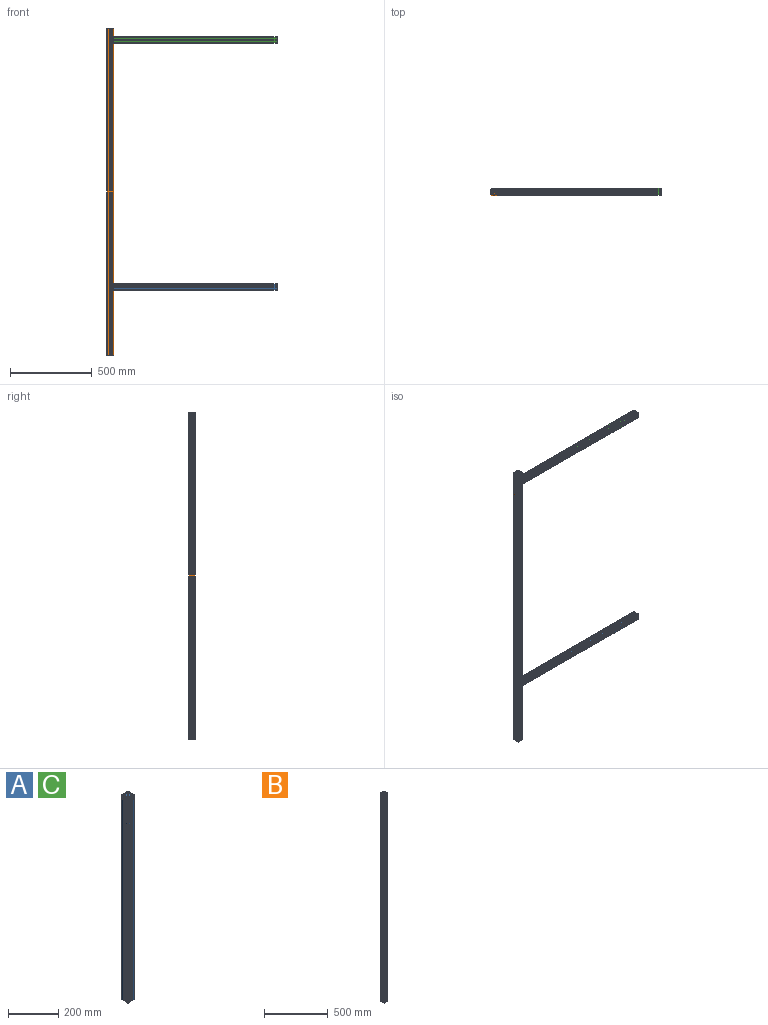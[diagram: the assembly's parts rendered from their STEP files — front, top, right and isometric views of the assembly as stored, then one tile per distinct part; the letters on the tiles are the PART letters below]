
ASSEMBLY  parts=3 mates=2
PART A: 147 faces, bbox 40x40x1000 mm
  f0: plane 1000x5.4mm, normal (1,0,0), area 5400mm2, adj f1,f7,f33,f146
  f1: cylinder r=0.5mm len=1000mm, axis (0,0,1), area 785.4mm2, adj f0,f2,f33,f146
  f2: plane 1000x5.4mm, normal (0,-1,0), area 5400mm2, adj f1,f3,f33,f146
  f3: cylinder r=0.5mm len=1000mm, axis (0,0,1), area 785.4mm2, adj f2,f4,f33,f146
  f4: plane 1000x3.7mm, normal (-1,0,0), area 3700mm2, adj f3,f5,f33,f146
  f5: cylinder r=2.2mm len=1000mm, axis (0,0,1), area 3455.8mm2, adj f4,f6,f33,f146
  f6: plane 1000x3.7mm, normal (0,1,0), area 3700mm2, adj f5,f7,f33,f146
  f7: cylinder r=0.5mm len=1000mm, axis (0,0,1), area 785.4mm2, adj f0,f6,f33,f146
  f8: plane 1000x5.4mm, normal (0,-1,0), area 5400mm2, adj f9,f15,f33,f146
  f9: cylinder r=0.5mm len=1000mm, axis (0,0,1), area 785.4mm2, adj f8,f10,f33,f146
  f10: plane 1000x5.4mm, normal (-1,0,0), area 5400mm2, adj f9,f11,f33,f146
  f11: cylinder r=0.5mm len=1000mm, axis (0,0,1), area 785.4mm2, adj f10,f12,f33,f146
  f12: plane 1000x3.7mm, normal (0,1,0), area 3700mm2, adj f11,f13,f33,f146
  f13: cylinder r=2.2mm len=1000mm, axis (0,0,1), area 3455.8mm2, adj f12,f14,f33,f146
  f14: plane 1000x3.7mm, normal (1,0,0), area 3700mm2, adj f13,f15,f33,f146
  f15: cylinder r=0.5mm len=1000mm, axis (0,0,1), area 785.4mm2, adj f8,f14,f33,f146
  f16: plane 1000x5.4mm, normal (-1,0,0), area 5400mm2, adj f17,f23,f33,f146
  f17: cylinder r=0.5mm len=1000mm, axis (0,0,1), area 785.4mm2, adj f16,f18,f33,f146
  f18: plane 1000x5.4mm, normal (0,1,0), area 5400mm2, adj f17,f19,f33,f146
  f19: cylinder r=0.5mm len=1000mm, axis (0,0,1), area 785.4mm2, adj f18,f20,f33,f146
  f20: plane 1000x3.7mm, normal (1,0,0), area 3700mm2, adj f19,f21,f33,f146
  f21: cylinder r=2.2mm len=1000mm, axis (0,0,1), area 3455.8mm2, adj f20,f22,f33,f146
  f22: plane 1000x3.7mm, normal (0,-1,0), area 3700mm2, adj f21,f23,f33,f146
  f23: cylinder r=0.5mm len=1000mm, axis (0,0,1), area 785.4mm2, adj f16,f22,f33,f146
  f24: plane 1000x5.4mm, normal (0,1,0), area 5400mm2, adj f25,f31,f33,f146
  f25: cylinder r=0.5mm len=1000mm, axis (0,0,1), area 785.4mm2, adj f24,f26,f33,f146
  f26: plane 1000x5.4mm, normal (1,0,0), area 5400mm2, adj f25,f27,f33,f146
  f27: cylinder r=0.5mm len=1000mm, axis (0,0,1), area 785.4mm2, adj f26,f28,f33,f146
  f28: plane 1000x3.7mm, normal (0,-1,0), area 3700mm2, adj f27,f29,f33,f146
  f29: cylinder r=2.2mm len=1000mm, axis (0,0,1), area 3455.8mm2, adj f28,f30,f33,f146
  f30: plane 1000x3.7mm, normal (-1,0,0), area 3700mm2, adj f29,f31,f33,f146
  f31: cylinder r=0.5mm len=1000mm, axis (0,0,1), area 785.4mm2, adj f24,f30,f33,f146
  f32: cylinder r=3.4mm len=1000mm, axis (0,0,1), area 21362.8mm2, adj f33,f146
  f33: plane 40x40mm, normal (0,0,-1), area 657.1mm2, adj f0,f1,f2,f3,f4,f5,f6,f7
  f34: cylinder r=1.5mm len=1000mm, axis (0,0,1), area 2356.2mm2, adj f33,f35,f145,f146
  f35: plane 1000x10.5mm, normal (-1,0,0), area 10500mm2, adj f33,f34,f36,f146
  f36: cylinder r=4mm len=1000mm, axis (0,0,1), area 6283.2mm2, adj f33,f35,f37,f146
  f37: plane 1000x10.5mm, normal (0,1,0), area 10500mm2, adj f33,f36,f38,f146
  f38: cylinder r=1.5mm len=1000mm, axis (0,0,1), area 2356.2mm2, adj f33,f37,f39,f146
  f39: plane 1000x2mm, normal (1,0,0), area 2000mm2, adj f33,f38,f40,f146
  f40: cylinder r=1mm len=1000mm, axis (0,0,1), area 1570.8mm2, adj f33,f39,f41,f146
  f41: plane 1000x1.5mm, normal (0,-1,0), area 1500mm2, adj f33,f40,f42,f146
  f42: cylinder r=0.5mm len=1000mm, axis (0,0,1), area 785.4mm2, adj f33,f41,f43,f146
  f43: plane 1000x1.5mm, normal (-1,0,0), area 1500mm2, adj f33,f42,f44,f146
  f44: cylinder r=0.5mm len=1000mm, axis (0,0,1), area 785.4mm2, adj f33,f43,f45,f146
  f45: cylinder r=2.5mm len=1000mm, axis (0,0,1), area 3927mm2, adj f33,f44,f46,f146
  f46: plane 1000x1.31mm, normal (1,0,0), area 1307.6mm2, adj f33,f45,f47,f146
  f47: cylinder r=5mm len=1000mm, axis (0,0,1), area 3927mm2, adj f33,f46,f48,f146
  f48: plane 1000x1.44mm, normal (0.71,0.71,0), area 2039.8mm2, adj f33,f47,f49,f146
  f49: cylinder r=5mm len=1000mm, axis (0,0,1), area 3927mm2, adj f33,f48,f50,f146
  f50: plane 1000x7.12mm, normal (0,1,0), area 7115.2mm2, adj f33,f49,f51,f146
  f51: cylinder r=5mm len=1000mm, axis (0,0,1), area 3927mm2, adj f33,f50,f52,f146
  f52: plane 1000x1.44mm, normal (-0.71,0.71,0), area 2039.8mm2, adj f33,f51,f53,f146
  f53: cylinder r=5mm len=1000mm, axis (0,0,1), area 3927mm2, adj f33,f52,f54,f146
  f54: plane 1000x1.31mm, normal (-1,0,0), area 1307.6mm2, adj f33,f53,f55,f146
  f55: cylinder r=2.5mm len=1000mm, axis (0,0,1), area 3927mm2, adj f33,f54,f56,f146
  f56: cylinder r=0.5mm len=1000mm, axis (0,0,1), area 785.4mm2, adj f33,f55,f57,f146
  f57: plane 1000x1.5mm, normal (1,0,0), area 1500mm2, adj f33,f56,f58,f146
  f58: cylinder r=0.5mm len=1000mm, axis (0,0,1), area 785.4mm2, adj f33,f57,f59,f146
  f59: plane 1000x1.5mm, normal (0,-1,0), area 1500mm2, adj f33,f58,f60,f146
  f60: cylinder r=1mm len=1000mm, axis (0,0,1), area 1570.8mm2, adj f33,f59,f61,f146
  f61: plane 1000x2mm, normal (-1,0,0), area 2000mm2, adj f33,f60,f62,f146
  f62: cylinder r=1.5mm len=1000mm, axis (0,0,1), area 2356.2mm2, adj f33,f61,f63,f146
  f63: plane 1000x10.5mm, normal (0,1,0), area 10500mm2, adj f33,f62,f64,f146
  f64: cylinder r=4mm len=1000mm, axis (0,0,1), area 6283.2mm2, adj f33,f63,f65,f146
  f65: plane 1000x10.5mm, normal (1,0,0), area 10500mm2, adj f33,f64,f66,f146
  f66: cylinder r=1.5mm len=1000mm, axis (0,0,1), area 2356.2mm2, adj f33,f65,f67,f146
  f67: plane 1000x2mm, normal (0,-1,0), area 2000mm2, adj f33,f66,f68,f146
  f68: cylinder r=1mm len=1000mm, axis (0,0,1), area 1570.8mm2, adj f33,f67,f69,f146
  f69: plane 1000x1.5mm, normal (-1,0,0), area 1500mm2, adj f33,f68,f70,f146
  f70: cylinder r=0.5mm len=1000mm, axis (0,0,1), area 785.4mm2, adj f33,f69,f71,f146
  f71: plane 1000x1.5mm, normal (0,1,0), area 1500mm2, adj f33,f70,f72,f146
  f72: cylinder r=0.5mm len=1000mm, axis (0,0,1), area 785.4mm2, adj f33,f71,f73,f146
  f73: cylinder r=2.5mm len=1000mm, axis (0,0,1), area 3927mm2, adj f33,f72,f74,f146
  f74: plane 1000x1.31mm, normal (0,-1,0), area 1307.6mm2, adj f33,f73,f75,f146
  f75: cylinder r=5mm len=1000mm, axis (0,0,1), area 3927mm2, adj f33,f74,f76,f146
  f76: plane 1000x1.44mm, normal (0.71,-0.71,0), area 2039.8mm2, adj f33,f75,f77,f146
  f77: cylinder r=5mm len=1000mm, axis (0,0,1), area 3927mm2, adj f33,f76,f78,f146
  f78: plane 1000x7.12mm, normal (1,0,0), area 7115.2mm2, adj f33,f77,f79,f146
  f79: cylinder r=5mm len=1000mm, axis (0,0,1), area 3927mm2, adj f33,f78,f80,f146
  f80: plane 1000x1.44mm, normal (0.71,0.71,0), area 2039.8mm2, adj f33,f79,f81,f146
  f81: cylinder r=5mm len=1000mm, axis (0,0,1), area 3927mm2, adj f33,f80,f82,f146
  f82: plane 1000x1.31mm, normal (0,1,0), area 1307.6mm2, adj f33,f81,f83,f146
  f83: cylinder r=2.5mm len=1000mm, axis (0,0,1), area 3927mm2, adj f33,f82,f84,f146
  f84: cylinder r=0.5mm len=1000mm, axis (0,0,1), area 785.4mm2, adj f33,f83,f85,f146
  f85: plane 1000x1.5mm, normal (0,-1,0), area 1500mm2, adj f33,f84,f86,f146
  f86: cylinder r=0.5mm len=1000mm, axis (0,0,1), area 785.4mm2, adj f33,f85,f87,f146
  f87: plane 1000x1.5mm, normal (-1,0,0), area 1500mm2, adj f33,f86,f88,f146
  f88: cylinder r=1mm len=1000mm, axis (0,0,1), area 1570.8mm2, adj f33,f87,f89,f146
  f89: plane 1000x2mm, normal (0,1,0), area 2000mm2, adj f33,f88,f90,f146
  f90: cylinder r=1.5mm len=1000mm, axis (0,0,1), area 2356.2mm2, adj f33,f89,f91,f146
  f91: plane 1000x10.5mm, normal (1,0,0), area 10500mm2, adj f33,f90,f92,f146
  f92: cylinder r=4mm len=1000mm, axis (0,0,1), area 6283.2mm2, adj f33,f91,f93,f146
  f93: plane 1000x10.5mm, normal (0,-1,0), area 10500mm2, adj f33,f92,f94,f146
  f94: cylinder r=1.5mm len=1000mm, axis (0,0,1), area 2356.2mm2, adj f33,f93,f95,f146
  f95: plane 1000x2mm, normal (-1,0,0), area 2000mm2, adj f33,f94,f96,f146
  f96: cylinder r=1mm len=1000mm, axis (0,0,1), area 1570.8mm2, adj f33,f95,f97,f146
  f97: plane 1000x1.5mm, normal (0,1,0), area 1500mm2, adj f33,f96,f98,f146
  f98: cylinder r=0.5mm len=1000mm, axis (0,0,1), area 785.4mm2, adj f33,f97,f99,f146
  f99: plane 1000x1.5mm, normal (1,0,0), area 1500mm2, adj f33,f98,f100,f146
  f100: cylinder r=0.5mm len=1000mm, axis (0,0,1), area 785.4mm2, adj f33,f99,f101,f146
  f101: cylinder r=2.5mm len=1000mm, axis (0,0,1), area 3927mm2, adj f33,f100,f102,f146
  f102: plane 1000x1.31mm, normal (-1,0,0), area 1307.6mm2, adj f33,f101,f103,f146
  f103: cylinder r=5mm len=1000mm, axis (0,0,1), area 3927mm2, adj f33,f102,f104,f146
  f104: plane 1000x1.44mm, normal (-0.71,-0.71,0), area 2039.8mm2, adj f33,f103,f105,f146
  f105: cylinder r=5mm len=1000mm, axis (0,0,1), area 3927mm2, adj f33,f104,f106,f146
  f106: plane 1000x7.12mm, normal (0,-1,0), area 7115.2mm2, adj f33,f105,f107,f146
  f107: cylinder r=5mm len=1000mm, axis (0,0,1), area 3927mm2, adj f33,f106,f108,f146
  f108: plane 1000x1.44mm, normal (0.71,-0.71,0), area 2039.8mm2, adj f33,f107,f109,f146
  f109: cylinder r=5mm len=1000mm, axis (0,0,1), area 3927mm2, adj f33,f108,f110,f146
  f110: plane 1000x1.31mm, normal (1,0,0), area 1307.6mm2, adj f33,f109,f111,f146
  f111: cylinder r=2.5mm len=1000mm, axis (0,0,1), area 3927mm2, adj f33,f110,f112,f146
  f112: cylinder r=0.5mm len=1000mm, axis (0,0,1), area 785.4mm2, adj f33,f111,f113,f146
  f113: plane 1000x1.5mm, normal (-1,0,0), area 1500mm2, adj f33,f112,f114,f146
  f114: cylinder r=0.5mm len=1000mm, axis (0,0,1), area 785.4mm2, adj f33,f113,f115,f146
  f115: plane 1000x1.5mm, normal (0,1,0), area 1500mm2, adj f33,f114,f116,f146
  f116: cylinder r=1mm len=1000mm, axis (0,0,1), area 1570.8mm2, adj f33,f115,f117,f146
  f117: plane 1000x2mm, normal (1,0,0), area 2000mm2, adj f33,f116,f118,f146
  f118: cylinder r=1.5mm len=1000mm, axis (0,0,1), area 2356.2mm2, adj f33,f117,f119,f146
  f119: plane 1000x10.5mm, normal (0,-1,0), area 10500mm2, adj f33,f118,f120,f146
  f120: cylinder r=4mm len=1000mm, axis (0,0,1), area 6283.2mm2, adj f33,f119,f121,f146
  f121: plane 1000x10.5mm, normal (-1,0,0), area 10500mm2, adj f33,f120,f122,f146
  f122: cylinder r=1.5mm len=1000mm, axis (0,0,1), area 2356.2mm2, adj f33,f121,f123,f146
  f123: plane 1000x2mm, normal (0,1,0), area 2000mm2, adj f33,f122,f124,f146
  f124: cylinder r=1mm len=1000mm, axis (0,0,1), area 1570.8mm2, adj f33,f123,f125,f146
  f125: plane 1000x1.5mm, normal (1,0,0), area 1500mm2, adj f33,f124,f126,f146
  f126: cylinder r=0.5mm len=1000mm, axis (0,0,1), area 785.4mm2, adj f33,f125,f127,f146
  f127: plane 1000x1.5mm, normal (0,-1,0), area 1500mm2, adj f33,f126,f128,f146
  f128: cylinder r=0.5mm len=1000mm, axis (0,0,1), area 785.4mm2, adj f33,f127,f129,f146
  f129: cylinder r=2.5mm len=1000mm, axis (0,0,1), area 3927mm2, adj f33,f128,f130,f146
  f130: plane 1000x1.31mm, normal (0,1,0), area 1307.6mm2, adj f33,f129,f131,f146
  f131: cylinder r=5mm len=1000mm, axis (0,0,1), area 3927mm2, adj f33,f130,f132,f146
  f132: plane 1000x1.44mm, normal (-0.71,0.71,0), area 2039.8mm2, adj f33,f131,f133,f146
  f133: cylinder r=5mm len=1000mm, axis (0,0,1), area 3927mm2, adj f33,f132,f134,f146
  f134: plane 1000x7.12mm, normal (-1,0,0), area 7115.2mm2, adj f33,f133,f135,f146
  f135: cylinder r=5mm len=1000mm, axis (0,0,1), area 3927mm2, adj f33,f134,f136,f146
  f136: plane 1000x1.44mm, normal (-0.71,-0.71,0), area 2039.8mm2, adj f33,f135,f137,f146
  f137: cylinder r=5mm len=1000mm, axis (0,0,1), area 3927mm2, adj f33,f136,f138,f146
  f138: plane 1000x1.31mm, normal (0,-1,0), area 1307.6mm2, adj f33,f137,f139,f146
  f139: cylinder r=2.5mm len=1000mm, axis (0,0,1), area 3927mm2, adj f33,f138,f140,f146
  f140: cylinder r=0.5mm len=1000mm, axis (0,0,1), area 785.4mm2, adj f33,f139,f141,f146
  f141: plane 1000x1.5mm, normal (0,1,0), area 1500mm2, adj f33,f140,f142,f146
  f142: cylinder r=0.5mm len=1000mm, axis (0,0,1), area 785.4mm2, adj f33,f141,f143,f146
  f143: plane 1000x1.5mm, normal (1,0,0), area 1500mm2, adj f33,f142,f144,f146
  f144: cylinder r=1mm len=1000mm, axis (0,0,1), area 1570.8mm2, adj f33,f143,f145,f146
  f145: plane 1000x2mm, normal (0,-1,0), area 2000mm2, adj f33,f34,f144,f146
  f146: plane 40x40mm, normal (0,0,1), area 657.1mm2, adj f0,f1,f2,f3,f4,f5,f6,f7
PART B: 147 faces, bbox 40x40x2000 mm
  f0: plane 2000x5.4mm, normal (1,0,0), area 10800mm2, adj f1,f7,f33,f146
  f1: cylinder r=0.5mm len=2000mm, axis (0,0,1), area 1570.8mm2, adj f0,f2,f33,f146
  f2: plane 2000x5.4mm, normal (0,-1,0), area 10800mm2, adj f1,f3,f33,f146
  f3: cylinder r=0.5mm len=2000mm, axis (0,0,1), area 1570.8mm2, adj f2,f4,f33,f146
  f4: plane 2000x3.7mm, normal (-1,0,0), area 7400mm2, adj f3,f5,f33,f146
  f5: cylinder r=2.2mm len=2000mm, axis (0,0,1), area 6911.5mm2, adj f4,f6,f33,f146
  f6: plane 2000x3.7mm, normal (0,1,0), area 7400mm2, adj f5,f7,f33,f146
  f7: cylinder r=0.5mm len=2000mm, axis (0,0,1), area 1570.8mm2, adj f0,f6,f33,f146
  f8: plane 2000x5.4mm, normal (0,-1,0), area 10800mm2, adj f9,f15,f33,f146
  f9: cylinder r=0.5mm len=2000mm, axis (0,0,1), area 1570.8mm2, adj f8,f10,f33,f146
  f10: plane 2000x5.4mm, normal (-1,0,0), area 10800mm2, adj f9,f11,f33,f146
  f11: cylinder r=0.5mm len=2000mm, axis (0,0,1), area 1570.8mm2, adj f10,f12,f33,f146
  f12: plane 2000x3.7mm, normal (0,1,0), area 7400mm2, adj f11,f13,f33,f146
  f13: cylinder r=2.2mm len=2000mm, axis (0,0,1), area 6911.5mm2, adj f12,f14,f33,f146
  f14: plane 2000x3.7mm, normal (1,0,0), area 7400mm2, adj f13,f15,f33,f146
  f15: cylinder r=0.5mm len=2000mm, axis (0,0,1), area 1570.8mm2, adj f8,f14,f33,f146
  f16: plane 2000x5.4mm, normal (-1,0,0), area 10800mm2, adj f17,f23,f33,f146
  f17: cylinder r=0.5mm len=2000mm, axis (0,0,1), area 1570.8mm2, adj f16,f18,f33,f146
  f18: plane 2000x5.4mm, normal (0,1,0), area 10800mm2, adj f17,f19,f33,f146
  f19: cylinder r=0.5mm len=2000mm, axis (0,0,1), area 1570.8mm2, adj f18,f20,f33,f146
  f20: plane 2000x3.7mm, normal (1,0,0), area 7400mm2, adj f19,f21,f33,f146
  f21: cylinder r=2.2mm len=2000mm, axis (0,0,1), area 6911.5mm2, adj f20,f22,f33,f146
  f22: plane 2000x3.7mm, normal (0,-1,0), area 7400mm2, adj f21,f23,f33,f146
  f23: cylinder r=0.5mm len=2000mm, axis (0,0,1), area 1570.8mm2, adj f16,f22,f33,f146
  f24: plane 2000x5.4mm, normal (0,1,0), area 10800mm2, adj f25,f31,f33,f146
  f25: cylinder r=0.5mm len=2000mm, axis (0,0,1), area 1570.8mm2, adj f24,f26,f33,f146
  f26: plane 2000x5.4mm, normal (1,0,0), area 10800mm2, adj f25,f27,f33,f146
  f27: cylinder r=0.5mm len=2000mm, axis (0,0,1), area 1570.8mm2, adj f26,f28,f33,f146
  f28: plane 2000x3.7mm, normal (0,-1,0), area 7400mm2, adj f27,f29,f33,f146
  f29: cylinder r=2.2mm len=2000mm, axis (0,0,1), area 6911.5mm2, adj f28,f30,f33,f146
  f30: plane 2000x3.7mm, normal (-1,0,0), area 7400mm2, adj f29,f31,f33,f146
  f31: cylinder r=0.5mm len=2000mm, axis (0,0,1), area 1570.8mm2, adj f24,f30,f33,f146
  f32: cylinder r=3.4mm len=2000mm, axis (0,0,1), area 42725.7mm2, adj f33,f146
  f33: plane 40x40mm, normal (0,0,-1), area 657.1mm2, adj f0,f1,f2,f3,f4,f5,f6,f7
  f34: cylinder r=1.5mm len=2000mm, axis (0,0,1), area 4712.4mm2, adj f33,f35,f145,f146
  f35: plane 2000x10.5mm, normal (-1,0,0), area 21000mm2, adj f33,f34,f36,f146
  f36: cylinder r=4mm len=2000mm, axis (0,0,1), area 12566.4mm2, adj f33,f35,f37,f146
  f37: plane 2000x10.5mm, normal (0,1,0), area 21000mm2, adj f33,f36,f38,f146
  f38: cylinder r=1.5mm len=2000mm, axis (0,0,1), area 4712.4mm2, adj f33,f37,f39,f146
  f39: plane 2000x2mm, normal (1,0,0), area 4000mm2, adj f33,f38,f40,f146
  f40: cylinder r=1mm len=2000mm, axis (0,0,1), area 3141.6mm2, adj f33,f39,f41,f146
  f41: plane 2000x1.5mm, normal (0,-1,0), area 3000mm2, adj f33,f40,f42,f146
  f42: cylinder r=0.5mm len=2000mm, axis (0,0,1), area 1570.8mm2, adj f33,f41,f43,f146
  f43: plane 2000x1.5mm, normal (-1,0,0), area 3000mm2, adj f33,f42,f44,f146
  f44: cylinder r=0.5mm len=2000mm, axis (0,0,1), area 1570.8mm2, adj f33,f43,f45,f146
  f45: cylinder r=2.5mm len=2000mm, axis (0,0,1), area 7854mm2, adj f33,f44,f46,f146
  f46: plane 2000x1.31mm, normal (1,0,0), area 2615.2mm2, adj f33,f45,f47,f146
  f47: cylinder r=5mm len=2000mm, axis (0,0,1), area 7854mm2, adj f33,f46,f48,f146
  f48: plane 2000x1.44mm, normal (0.71,0.71,0), area 4079.7mm2, adj f33,f47,f49,f146
  f49: cylinder r=5mm len=2000mm, axis (0,0,1), area 7854mm2, adj f33,f48,f50,f146
  f50: plane 2000x7.12mm, normal (0,1,0), area 14230.4mm2, adj f33,f49,f51,f146
  f51: cylinder r=5mm len=2000mm, axis (0,0,1), area 7854mm2, adj f33,f50,f52,f146
  f52: plane 2000x1.44mm, normal (-0.71,0.71,0), area 4079.7mm2, adj f33,f51,f53,f146
  f53: cylinder r=5mm len=2000mm, axis (0,0,1), area 7854mm2, adj f33,f52,f54,f146
  f54: plane 2000x1.31mm, normal (-1,0,0), area 2615.2mm2, adj f33,f53,f55,f146
  f55: cylinder r=2.5mm len=2000mm, axis (0,0,1), area 7854mm2, adj f33,f54,f56,f146
  f56: cylinder r=0.5mm len=2000mm, axis (0,0,1), area 1570.8mm2, adj f33,f55,f57,f146
  f57: plane 2000x1.5mm, normal (1,0,0), area 3000mm2, adj f33,f56,f58,f146
  f58: cylinder r=0.5mm len=2000mm, axis (0,0,1), area 1570.8mm2, adj f33,f57,f59,f146
  f59: plane 2000x1.5mm, normal (0,-1,0), area 3000mm2, adj f33,f58,f60,f146
  f60: cylinder r=1mm len=2000mm, axis (0,0,1), area 3141.6mm2, adj f33,f59,f61,f146
  f61: plane 2000x2mm, normal (-1,0,0), area 4000mm2, adj f33,f60,f62,f146
  f62: cylinder r=1.5mm len=2000mm, axis (0,0,1), area 4712.4mm2, adj f33,f61,f63,f146
  f63: plane 2000x10.5mm, normal (0,1,0), area 21000mm2, adj f33,f62,f64,f146
  f64: cylinder r=4mm len=2000mm, axis (0,0,1), area 12566.4mm2, adj f33,f63,f65,f146
  f65: plane 2000x10.5mm, normal (1,0,0), area 21000mm2, adj f33,f64,f66,f146
  f66: cylinder r=1.5mm len=2000mm, axis (0,0,1), area 4712.4mm2, adj f33,f65,f67,f146
  f67: plane 2000x2mm, normal (0,-1,0), area 4000mm2, adj f33,f66,f68,f146
  f68: cylinder r=1mm len=2000mm, axis (0,0,1), area 3141.6mm2, adj f33,f67,f69,f146
  f69: plane 2000x1.5mm, normal (-1,0,0), area 3000mm2, adj f33,f68,f70,f146
  f70: cylinder r=0.5mm len=2000mm, axis (0,0,1), area 1570.8mm2, adj f33,f69,f71,f146
  f71: plane 2000x1.5mm, normal (0,1,0), area 3000mm2, adj f33,f70,f72,f146
  f72: cylinder r=0.5mm len=2000mm, axis (0,0,1), area 1570.8mm2, adj f33,f71,f73,f146
  f73: cylinder r=2.5mm len=2000mm, axis (0,0,1), area 7854mm2, adj f33,f72,f74,f146
  f74: plane 2000x1.31mm, normal (0,-1,0), area 2615.2mm2, adj f33,f73,f75,f146
  f75: cylinder r=5mm len=2000mm, axis (0,0,1), area 7854mm2, adj f33,f74,f76,f146
  f76: plane 2000x1.44mm, normal (0.71,-0.71,0), area 4079.7mm2, adj f33,f75,f77,f146
  f77: cylinder r=5mm len=2000mm, axis (0,0,1), area 7854mm2, adj f33,f76,f78,f146
  f78: plane 2000x7.12mm, normal (1,0,0), area 14230.4mm2, adj f33,f77,f79,f146
  f79: cylinder r=5mm len=2000mm, axis (0,0,1), area 7854mm2, adj f33,f78,f80,f146
  f80: plane 2000x1.44mm, normal (0.71,0.71,0), area 4079.7mm2, adj f33,f79,f81,f146
  f81: cylinder r=5mm len=2000mm, axis (0,0,1), area 7854mm2, adj f33,f80,f82,f146
  f82: plane 2000x1.31mm, normal (0,1,0), area 2615.2mm2, adj f33,f81,f83,f146
  f83: cylinder r=2.5mm len=2000mm, axis (0,0,1), area 7854mm2, adj f33,f82,f84,f146
  f84: cylinder r=0.5mm len=2000mm, axis (0,0,1), area 1570.8mm2, adj f33,f83,f85,f146
  f85: plane 2000x1.5mm, normal (0,-1,0), area 3000mm2, adj f33,f84,f86,f146
  f86: cylinder r=0.5mm len=2000mm, axis (0,0,1), area 1570.8mm2, adj f33,f85,f87,f146
  f87: plane 2000x1.5mm, normal (-1,0,0), area 3000mm2, adj f33,f86,f88,f146
  f88: cylinder r=1mm len=2000mm, axis (0,0,1), area 3141.6mm2, adj f33,f87,f89,f146
  f89: plane 2000x2mm, normal (0,1,0), area 4000mm2, adj f33,f88,f90,f146
  f90: cylinder r=1.5mm len=2000mm, axis (0,0,1), area 4712.4mm2, adj f33,f89,f91,f146
  f91: plane 2000x10.5mm, normal (1,0,0), area 21000mm2, adj f33,f90,f92,f146
  f92: cylinder r=4mm len=2000mm, axis (0,0,1), area 12566.4mm2, adj f33,f91,f93,f146
  f93: plane 2000x10.5mm, normal (0,-1,0), area 21000mm2, adj f33,f92,f94,f146
  f94: cylinder r=1.5mm len=2000mm, axis (0,0,1), area 4712.4mm2, adj f33,f93,f95,f146
  f95: plane 2000x2mm, normal (-1,0,0), area 4000mm2, adj f33,f94,f96,f146
  f96: cylinder r=1mm len=2000mm, axis (0,0,1), area 3141.6mm2, adj f33,f95,f97,f146
  f97: plane 2000x1.5mm, normal (0,1,0), area 3000mm2, adj f33,f96,f98,f146
  f98: cylinder r=0.5mm len=2000mm, axis (0,0,1), area 1570.8mm2, adj f33,f97,f99,f146
  f99: plane 2000x1.5mm, normal (1,0,0), area 3000mm2, adj f33,f98,f100,f146
  f100: cylinder r=0.5mm len=2000mm, axis (0,0,1), area 1570.8mm2, adj f33,f99,f101,f146
  f101: cylinder r=2.5mm len=2000mm, axis (0,0,1), area 7854mm2, adj f33,f100,f102,f146
  f102: plane 2000x1.31mm, normal (-1,0,0), area 2615.2mm2, adj f33,f101,f103,f146
  f103: cylinder r=5mm len=2000mm, axis (0,0,1), area 7854mm2, adj f33,f102,f104,f146
  f104: plane 2000x1.44mm, normal (-0.71,-0.71,0), area 4079.7mm2, adj f33,f103,f105,f146
  f105: cylinder r=5mm len=2000mm, axis (0,0,1), area 7854mm2, adj f33,f104,f106,f146
  f106: plane 2000x7.12mm, normal (0,-1,0), area 14230.4mm2, adj f33,f105,f107,f146
  f107: cylinder r=5mm len=2000mm, axis (0,0,1), area 7854mm2, adj f33,f106,f108,f146
  f108: plane 2000x1.44mm, normal (0.71,-0.71,0), area 4079.7mm2, adj f33,f107,f109,f146
  f109: cylinder r=5mm len=2000mm, axis (0,0,1), area 7854mm2, adj f33,f108,f110,f146
  f110: plane 2000x1.31mm, normal (1,0,0), area 2615.2mm2, adj f33,f109,f111,f146
  f111: cylinder r=2.5mm len=2000mm, axis (0,0,1), area 7854mm2, adj f33,f110,f112,f146
  f112: cylinder r=0.5mm len=2000mm, axis (0,0,1), area 1570.8mm2, adj f33,f111,f113,f146
  f113: plane 2000x1.5mm, normal (-1,0,0), area 3000mm2, adj f33,f112,f114,f146
  f114: cylinder r=0.5mm len=2000mm, axis (0,0,1), area 1570.8mm2, adj f33,f113,f115,f146
  f115: plane 2000x1.5mm, normal (0,1,0), area 3000mm2, adj f33,f114,f116,f146
  f116: cylinder r=1mm len=2000mm, axis (0,0,1), area 3141.6mm2, adj f33,f115,f117,f146
  f117: plane 2000x2mm, normal (1,0,0), area 4000mm2, adj f33,f116,f118,f146
  f118: cylinder r=1.5mm len=2000mm, axis (0,0,1), area 4712.4mm2, adj f33,f117,f119,f146
  f119: plane 2000x10.5mm, normal (0,-1,0), area 21000mm2, adj f33,f118,f120,f146
  f120: cylinder r=4mm len=2000mm, axis (0,0,1), area 12566.4mm2, adj f33,f119,f121,f146
  f121: plane 2000x10.5mm, normal (-1,0,0), area 21000mm2, adj f33,f120,f122,f146
  f122: cylinder r=1.5mm len=2000mm, axis (0,0,1), area 4712.4mm2, adj f33,f121,f123,f146
  f123: plane 2000x2mm, normal (0,1,0), area 4000mm2, adj f33,f122,f124,f146
  f124: cylinder r=1mm len=2000mm, axis (0,0,1), area 3141.6mm2, adj f33,f123,f125,f146
  f125: plane 2000x1.5mm, normal (1,0,0), area 3000mm2, adj f33,f124,f126,f146
  f126: cylinder r=0.5mm len=2000mm, axis (0,0,1), area 1570.8mm2, adj f33,f125,f127,f146
  f127: plane 2000x1.5mm, normal (0,-1,0), area 3000mm2, adj f33,f126,f128,f146
  f128: cylinder r=0.5mm len=2000mm, axis (0,0,1), area 1570.8mm2, adj f33,f127,f129,f146
  f129: cylinder r=2.5mm len=2000mm, axis (0,0,1), area 7854mm2, adj f33,f128,f130,f146
  f130: plane 2000x1.31mm, normal (0,1,0), area 2615.2mm2, adj f33,f129,f131,f146
  f131: cylinder r=5mm len=2000mm, axis (0,0,1), area 7854mm2, adj f33,f130,f132,f146
  f132: plane 2000x1.44mm, normal (-0.71,0.71,0), area 4079.7mm2, adj f33,f131,f133,f146
  f133: cylinder r=5mm len=2000mm, axis (0,0,1), area 7854mm2, adj f33,f132,f134,f146
  f134: plane 2000x7.12mm, normal (-1,0,0), area 14230.4mm2, adj f33,f133,f135,f146
  f135: cylinder r=5mm len=2000mm, axis (0,0,1), area 7854mm2, adj f33,f134,f136,f146
  f136: plane 2000x1.44mm, normal (-0.71,-0.71,0), area 4079.7mm2, adj f33,f135,f137,f146
  f137: cylinder r=5mm len=2000mm, axis (0,0,1), area 7854mm2, adj f33,f136,f138,f146
  f138: plane 2000x1.31mm, normal (0,-1,0), area 2615.2mm2, adj f33,f137,f139,f146
  f139: cylinder r=2.5mm len=2000mm, axis (0,0,1), area 7854mm2, adj f33,f138,f140,f146
  f140: cylinder r=0.5mm len=2000mm, axis (0,0,1), area 1570.8mm2, adj f33,f139,f141,f146
  f141: plane 2000x1.5mm, normal (0,1,0), area 3000mm2, adj f33,f140,f142,f146
  f142: cylinder r=0.5mm len=2000mm, axis (0,0,1), area 1570.8mm2, adj f33,f141,f143,f146
  f143: plane 2000x1.5mm, normal (1,0,0), area 3000mm2, adj f33,f142,f144,f146
  f144: cylinder r=1mm len=2000mm, axis (0,0,1), area 3141.6mm2, adj f33,f143,f145,f146
  f145: plane 2000x2mm, normal (0,-1,0), area 4000mm2, adj f33,f34,f144,f146
  f146: plane 40x40mm, normal (0,0,1), area 657.1mm2, adj f0,f1,f2,f3,f4,f5,f6,f7
PART C: same geometry as A
PLACE A rot(axis=(-0.58,-0.58,0.58),120deg) t=(402.77,-56.15,-259.59)mm
PLACE B t=(-467.23,-56.15,-529.59)mm
PLACE C rot(axis=(0.58,-0.58,-0.58),120deg) t=(402.77,-56.15,1250.41)mm
MATE fastened C.f146 <-> B.f65  axis (-1,0,0) through (-447.23,-40.15,1270.41)mm
MATE fastened A.f146 <-> B.f65  axis (-1,0,0) through (-447.23,-40.15,-279.59)mm
